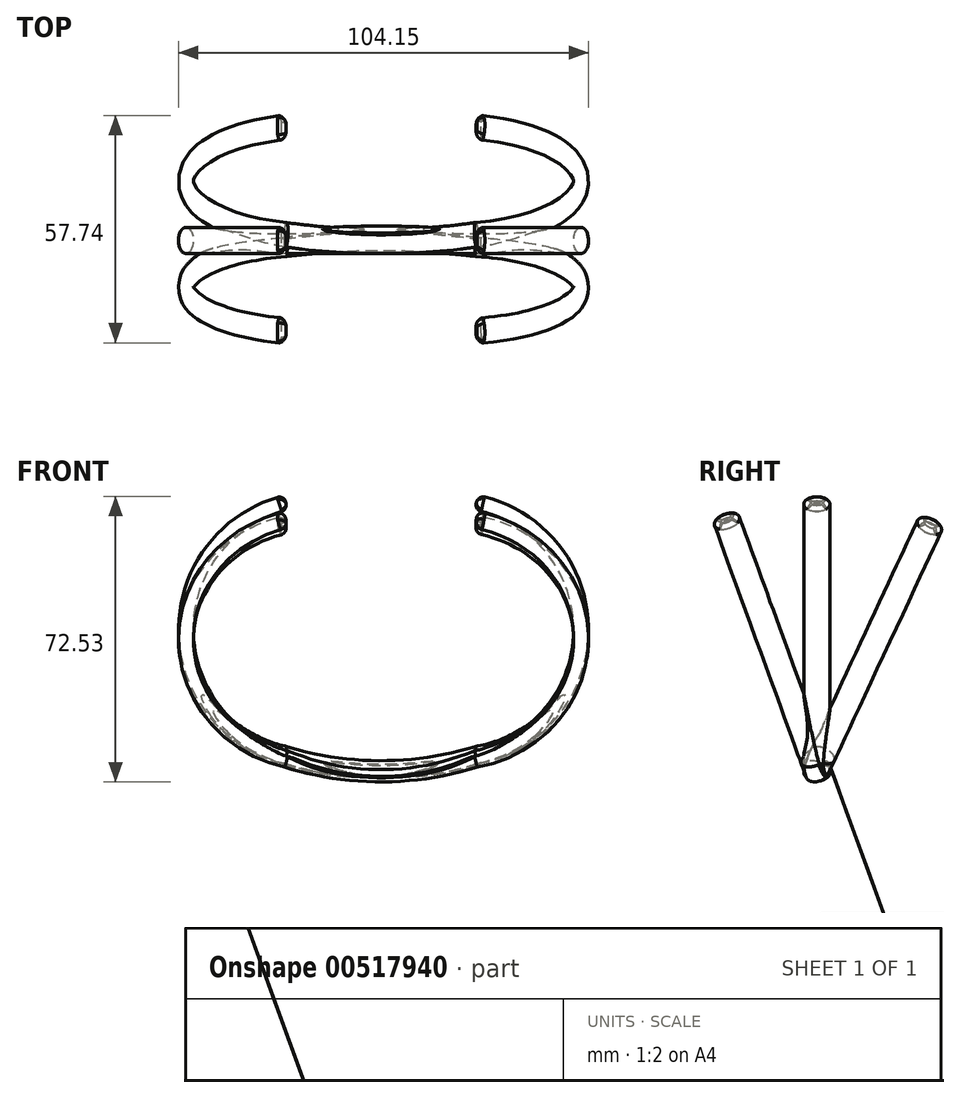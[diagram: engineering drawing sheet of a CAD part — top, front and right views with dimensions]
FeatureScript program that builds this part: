
annotation { "Feature Type Name" : "Feature", "Feature Type Description" : "" }
export const myFeature = defineFeature(function(context is Context, id is Id, definition is map)
    precondition{}
    {
        {
            var Q0;
            Q0=qCreatedBy(makeId("Front.planeOp"),FACE);
            var sketch = newSketch(context, id + "F0", { "sketchPlane" : qUnion([Q0])});
            skArc(sketch, "E0", {"start": v(0, 32.29) * mm, "mid": v(-25.39, 0) * mm, "end": v(0, -32.29) * mm});
            skArc(sketch, "E1", {"start": v(0, -32.29) * mm, "mid": v(24.16, -36.26) * mm, "end": v(48.32, -32.29) * mm});
            skArc(sketch, "E2", {"start": v(48.32, -32.29) * mm, "mid": v(74.94, 0) * mm, "end": v(48.32, 32.29) * mm});
            skSolve(sketch);
        }
        {
            var Q0;
            Q0=qCreatedBy(makeId("Right.planeOp"),FACE);
            var sketch = newSketch(context, id + "F1", { "sketchPlane" : qUnion([Q0])});
            skEllipse(sketch, "E3", {"center": v(0, 32.31) * mm, "majorRadius": 3.32 * mm, "minorRadius": 1.94 * mm, "majorAxis": v(1, 0)});
            skSolve(sketch);
        }
        {
            var Q0;
            Q0=makeQuery(id+"F1.imprint","IMPRINT",FACE,{"disambiguationData":[TD([[makeQuery(id+"F1.imprint","IMPRINT",EDGE,{"derivedFrom":sQuery(id+"F1.wireOp",EDGE,"E3")}),1.0]])]});
            var Q1;
            Q1=sQuery(id+"F1.wireOp",EDGE,"E3");
            var Q2;
            Q2=sQuery(id+"F0.wireOp",EDGE,"E0");
            var Q3;
            Q3=sQuery(id+"F0.wireOp",EDGE,"E1");
            var Q4;
            Q4=sQuery(id+"F0.wireOp",EDGE,"E2");
            sweep(context, id + "F2", {"profiles" : qUnion([Q0]), "surfaceProfiles" : qUnion([Q1]), "path" : qUnion([Q2, Q3, Q4])});
        }
        {
            var Q0;
            Q0=makeQuery(id+"F2.opSweep","CAP_FACE",FACE,{"disambiguationData":[OSD([sQuery(id+"F0.wireOp",VERTEX,"E2.end"),sQuery(id+"F1.wireOp",EDGE,"E3")])],"isStart":false});
            var Q1;
            Q1=makeQuery(id+"F2.opSweep","CAP_EDGE",EDGE,{"disambiguationData":[OSD([sQuery(id+"F0.wireOp",VERTEX,"E0.start"),sQuery(id+"F1.wireOp",EDGE,"E3")])],"isStart":true});
            fillet(context, id + "F3", {"entities" : qUnion([Q0, Q1]), "radius" : 1.7 * mm, "tangentPropagation" : true, "allowEdgeOverflow" : false});
        }
        {
            var Q0;
            Q0=makeQuery(id+"F2.opSweep","SWEPT_BODY",BODY,{"disambiguationData":[OSD([sQuery(id+"F0.wireOp",EDGE,"E2"),sQuery(id+"F1.wireOp",EDGE,"E3")])]});
            transform(context, id + "F4", {"entities" : qUnion([Q0]), "transformType" : TransformType.COPY});
        }
        {
            var Q0;
            Q0=qCreatedBy(makeId("Right.planeOp"),FACE);
            var sketch = newSketch(context, id + "F5", { "sketchPlane" : qUnion([Q0])});
            skCircle(sketch, "E4", {"center": v(21.39, 0) * mm, "radius": 4.15 * mm});
            skSolve(sketch);
        }
        {
            var Q0;
            Q0=makeQuery(id+"F2.opSweep","SWEPT_BODY",BODY,{"disambiguationData":[OSD([sQuery(id+"F0.wireOp",EDGE,"E2"),sQuery(id+"F1.wireOp",EDGE,"E3")])]});
            var Q1;
            Q1=sQuery(id+"F5.wireOp",EDGE,"E4");
            transform(context, id + "F6", {"entities" : qUnion([Q0]), "transformType" : TransformType.ROTATION, "transformAxis" : qUnion([Q1]), "angle" : 20 * degree, "makeCopy" : false});
        }
        {
            var Q0;
            Q0=makeQuery(id+"F2.opSweep","SWEPT_BODY",BODY,{"disambiguationData":[OSD([sQuery(id+"F0.wireOp",EDGE,"E2"),sQuery(id+"F1.wireOp",EDGE,"E3")])]});
            transform(context, id + "F7", {"entities" : qUnion([Q0]), "transformType" : TransformType.TRANSLATION_3D, "dx" : 0 * mm, "dy" : -13.2 * mm, "dz" : 4.9 * mm, "makeCopy" : false});
        }
        {
            var Q0;
            Q0=makeQuery(id+"F4.opPattern","COPY",BODY,{"derivedFrom":makeQuery(id+"F2.opSweep","SWEPT_BODY",BODY,{"disambiguationData":[OSD([sQuery(id+"F0.wireOp",EDGE,"E2"),sQuery(id+"F1.wireOp",EDGE,"E3")])]}),"instanceName":"1"});
            transform(context, id + "F8", {"entities" : qUnion([Q0]), "transformType" : TransformType.COPY});
        }
        {
            var Q0;
            Q0=makeQuery(id+"F4.opPattern","COPY",BODY,{"derivedFrom":makeQuery(id+"F2.opSweep","SWEPT_BODY",BODY,{"disambiguationData":[OSD([sQuery(id+"F0.wireOp",EDGE,"E2"),sQuery(id+"F1.wireOp",EDGE,"E3")])]}),"instanceName":"1"});
            var Q1;
            Q1=sQuery(id+"F5.wireOp",EDGE,"E4");
            transform(context, id + "F9", {"entities" : qUnion([Q0]), "transformType" : TransformType.ROTATION, "transformAxis" : qUnion([Q1]), "angle" : 25 * degree, "oppositeDirection" : true, "makeCopy" : false});
        }
        {
            var Q0;
            Q0=makeQuery(id+"F4.opPattern","COPY",BODY,{"derivedFrom":makeQuery(id+"F2.opSweep","SWEPT_BODY",BODY,{"disambiguationData":[OSD([sQuery(id+"F0.wireOp",EDGE,"E2"),sQuery(id+"F1.wireOp",EDGE,"E3")])]}),"instanceName":"1"});
            transform(context, id + "F10", {"entities" : qUnion([Q0]), "transformType" : TransformType.TRANSLATION_3D, "dx" : 0 * mm, "dy" : 13.1 * mm, "dz" : -11.6 * mm, "makeCopy" : false});
        }
        {
            var Q0;
            Q0=makeQuery(id+"F2.opSweep","SWEPT_BODY",BODY,{"disambiguationData":[OSD([sQuery(id+"F0.wireOp",EDGE,"E2"),sQuery(id+"F1.wireOp",EDGE,"E3")])]});
            var Q1;
            Q1=makeQuery(id+"F4.opPattern","COPY",BODY,{"derivedFrom":makeQuery(id+"F2.opSweep","SWEPT_BODY",BODY,{"disambiguationData":[OSD([sQuery(id+"F0.wireOp",EDGE,"E2"),sQuery(id+"F1.wireOp",EDGE,"E3")])]}),"instanceName":"1"});
            var Q2;
            Q2=makeQuery(id+"F8.opPattern","COPY",BODY,{"derivedFrom":makeQuery(id+"F4.opPattern","COPY",BODY,{"derivedFrom":makeQuery(id+"F2.opSweep","SWEPT_BODY",BODY,{"disambiguationData":[OSD([sQuery(id+"F0.wireOp",EDGE,"E2"),sQuery(id+"F1.wireOp",EDGE,"E3")])]}),"instanceName":"1"}),"instanceName":"1"});
            booleanBodies(context, id + "F11", {"operationType" : BooleanOperationType.UNION, "tools" : qUnion([Q0, Q1, Q2])});
        }
        {
            var Q0;
            {var subQ0=makeQuery(id+"F2.opSweep","SWEPT_FACE",FACE,{"disambiguationData":[OSD([sQuery(id+"F0.wireOp",EDGE,"E1"),sQuery(id+"F1.wireOp",EDGE,"E3")])]});Q0=makeQuery(id+"F11.opBoolean","INTERSECT",EDGE,{"derivedFrom":[subQ0,makeQuery(id+"F4.opPattern","COPY",FACE,{"derivedFrom":subQ0,"instanceName":"1"})]});}
            var Q1;
            {var subQ0=makeQuery(id+"F2.opSweep","SWEPT_FACE",FACE,{"disambiguationData":[OSD([sQuery(id+"F0.wireOp",EDGE,"E1"),sQuery(id+"F1.wireOp",EDGE,"E3")])]});Q1=makeQuery(id+"F11.opBoolean","INTERSECT",EDGE,{"disambiguationData":[OD(2.0)],"derivedFrom":[subQ0,makeQuery(id+"F8.opPattern","COPY",FACE,{"derivedFrom":makeQuery(id+"F4.opPattern","COPY",FACE,{"derivedFrom":subQ0,"instanceName":"1"}),"instanceName":"1"})]});}
            chamfer(context, id + "F12", {"entities" : qUnion([Q0, Q1]), "width" : 1 * mm, "tangentPropagation" : true});
        }
    });
